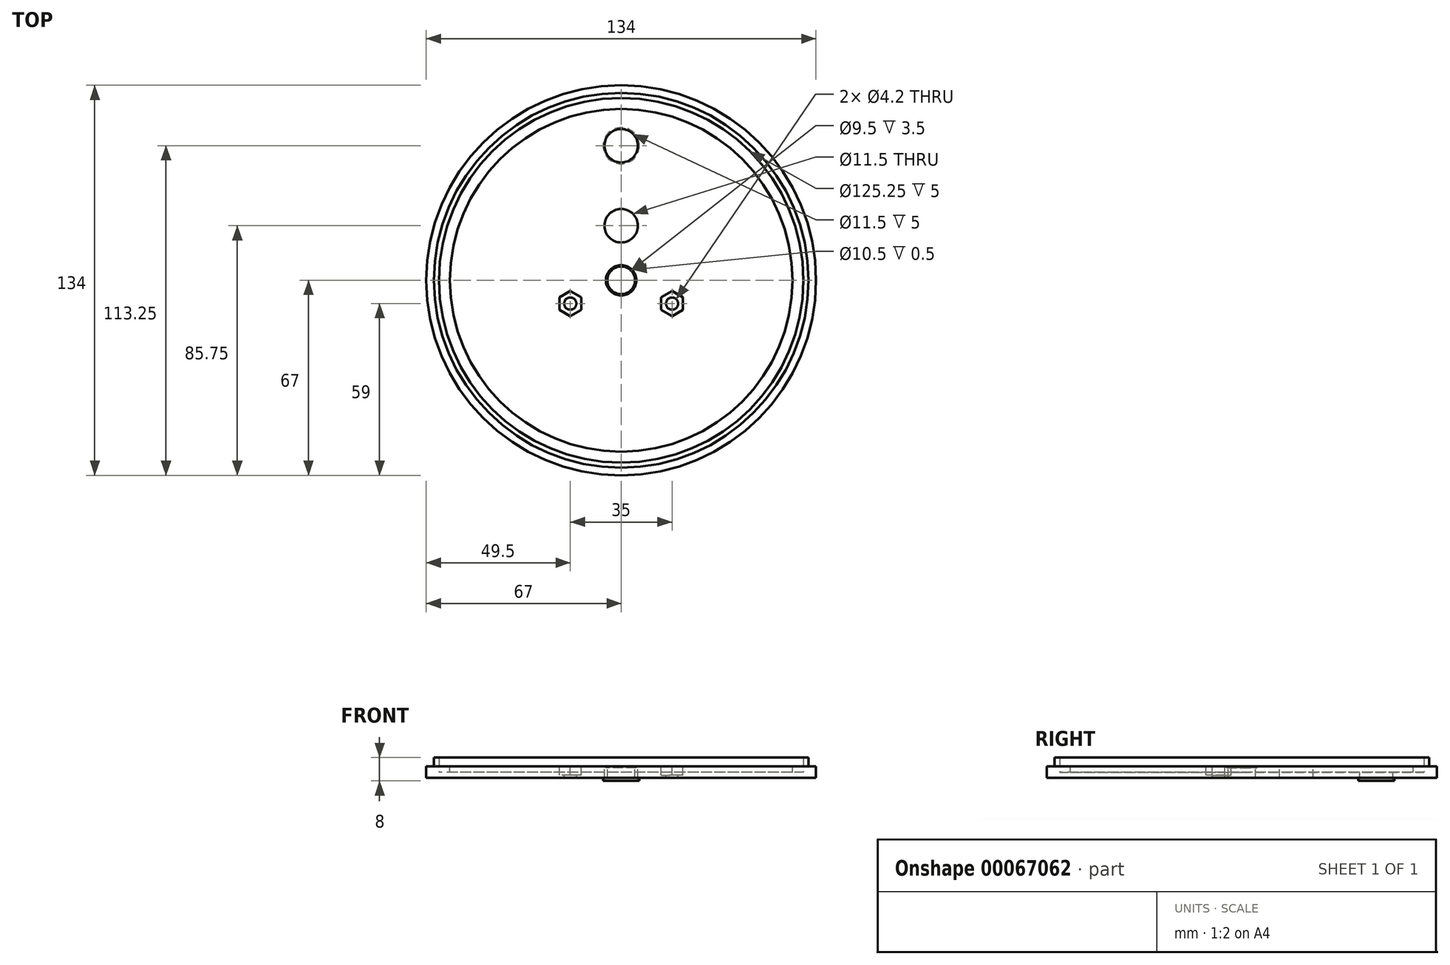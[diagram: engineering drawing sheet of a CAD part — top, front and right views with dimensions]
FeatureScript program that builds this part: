
annotation { "Feature Type Name" : "Feature", "Feature Type Description" : "" }
export const myFeature = defineFeature(function(context is Context, id is Id, definition is map)
    precondition{}
    {
        {
            var Q0;
            Q0=qCreatedBy(makeId("Top.planeOp"),FACE);
            var sketch = newSketch(context, id + "F0", { "sketchPlane" : qUnion([Q0])});
            skCircle(sketch, "E0", {"center": v(0, 0) * mm, "radius": 67 * mm});
            skSolve(sketch);
        }
        {
            var Q0;
            Q0=makeQuery(id+"F0.imprint","IMPRINT",FACE,{"disambiguationData":[TD([[makeQuery(id+"F0.imprint","IMPRINT",EDGE,{"derivedFrom":sQuery(id+"F0.wireOp",EDGE,"E0")}),1.0]])]});
            extrude(context, id + "F1", {"entities" : qUnion([Q0]), "endBound" : BoundingType.SYMMETRIC, "depth" : 5 * mm});
        }
        {
            var Q0;
            Q0=makeQuery(id+"F1.opExtrude","CAP_FACE",FACE,{"disambiguationData":[OSD([sQuery(id+"F0.wireOp",EDGE,"E0")])],"isStart":false});
            var sketch = newSketch(context, id + "F2", { "sketchPlane" : qUnion([Q0])});
            skCircle(sketch, "E1", {"center": v(0, 0) * mm, "radius": 64.38 * mm});
            skCircle(sketch, "E2", {"center": v(0, 0) * mm, "radius": 62.62 * mm});
            skCircle(sketch, "E3", {"center": v(0, 0) * mm, "radius": 58.88 * mm});
            skSolve(sketch);
        }
        {
            var Q0;
            Q0=makeQuery(id+"F2.imprint","IMPRINT",FACE,{"disambiguationData":[TD([[makeQuery(id+"F2.imprint","IMPRINT",EDGE,{"derivedFrom":sQuery(id+"F2.wireOp",EDGE,"E1")}),1.0]])]});
            var Q1;
            Q1=sQuery(id+"F2.wireOp",EDGE,"E1");
            var Q2;
            Q2=sQuery(id+"F2.wireOp",EDGE,"E2");
            extrude(context, id + "F3", {"entities" : qUnion([Q0]), "operationType" : NewBodyOperationType.ADD, "surfaceEntities" : qUnion([Q1, Q2]), "depth" : 3 * mm});
        }
        {
            var Q0;
            Q0=makeQuery(id+"F2.imprint","IMPRINT",FACE,{"disambiguationData":[TD([[makeQuery(id+"F2.imprint","IMPRINT",EDGE,{"derivedFrom":sQuery(id+"F2.wireOp",EDGE,"E2")}),1.0]])]});
            var Q1;
            Q1=sQuery(id+"F2.wireOp",EDGE,"E2");
            var Q2;
            Q2=sQuery(id+"F2.wireOp",EDGE,"E3");
            extrude(context, id + "F4", {"entities" : qUnion([Q0]), "operationType" : NewBodyOperationType.REMOVE, "surfaceEntities" : qUnion([Q1, Q2]), "oppositeDirection" : true, "depth" : 2 * mm});
        }
        {
            var Q0;
            Q0=makeQuery(id+"F2.imprint","IMPRINT",FACE,{"disambiguationData":[TD([[makeQuery(id+"F2.imprint","IMPRINT",EDGE,{"derivedFrom":sQuery(id+"F2.wireOp",EDGE,"E3")}),1.0]])]});
            var sketch = newSketch(context, id + "F5", { "sketchPlane" : qUnion([Q0])});
            skCircle(sketch, "E4", {"center": v(0, 0) * mm, "radius": 4.75 * mm});
            skCircle(sketch, "E5", {"center": v(0, 18.75) * mm, "radius": 5.75 * mm});
            skCircle(sketch, "E6", {"center": v(0, 46.25) * mm, "radius": 5.75 * mm});
            skLineSegment(sketch, "E7", {"start": v(0, -8) * mm, "end": v(17.5, -8) * mm, "construction": true});
            skCircle(sketch, "E8", {"center": v(17.5, -8) * mm, "radius": 2.1 * mm});
            skLineSegment(sketch, "E9", {"start": v(0, 0) * mm, "end": v(0, -8) * mm, "construction": true});
            skCircle(sketch, "E10.MirrorC", {"center": v(-17.5, -8) * mm, "radius": 2.1 * mm});
            skSolve(sketch);
        }
        {
            var Q0;
            Q0 = qSketchRegion(id + "F5", true);
            extrude(context, id + "F6", {"entities" : qUnion([Q0]), "operationType" : NewBodyOperationType.REMOVE, "endBound" : BoundingType.THROUGH_ALL, "oppositeDirection" : true, "depth" : 25 * mm});
        }
        {
            var Q0;
            Q0=makeQuery(id+"F2.imprint","IMPRINT",FACE,{"disambiguationData":[TD([[makeQuery(id+"F2.imprint","IMPRINT",EDGE,{"derivedFrom":sQuery(id+"F2.wireOp",EDGE,"E3")}),1.0]])]});
            var sketch = newSketch(context, id + "F7", { "sketchPlane" : qUnion([Q0])});
            skCircle(sketch, "E11", {"center": v(0, 46.25) * mm, "radius": 6.25 * mm});
            skCircle(sketch, "E12", {"center": v(0, 18.75) * mm, "radius": 6.25 * mm});
            skCircle(sketch, "E13", {"center": v(0, 0) * mm, "radius": 5.25 * mm});
            skCircle(sketch, "E14.cCircle", {"center": v(17.5, -8) * mm, "radius": 3.75 * mm, "construction": true});
            skLineSegment(sketch, "E14.0", {"start": v(21.25, -10.17) * mm, "end": v(17.5, -12.33) * mm});
            skLineSegment(sketch, "E14.1", {"start": v(17.5, -12.33) * mm, "end": v(13.75, -10.17) * mm});
            skLineSegment(sketch, "E14.2", {"start": v(13.75, -10.17) * mm, "end": v(13.75, -5.83) * mm});
            skLineSegment(sketch, "E14.3", {"start": v(13.75, -5.83) * mm, "end": v(17.5, -3.67) * mm});
            skLineSegment(sketch, "E14.4", {"start": v(17.5, -3.67) * mm, "end": v(21.25, -5.83) * mm});
            skLineSegment(sketch, "E14.5", {"start": v(21.25, -5.83) * mm, "end": v(21.25, -10.17) * mm});
            skPoint(sketch, "E14.0.midPoint", {"position": v(19.38, -11.25) * mm});
            skLineSegment(sketch, "E15.MirrorCS", {"start": v(-13.75, -5.83) * mm, "end": v(-17.5, -3.67) * mm});
            skLineSegment(sketch, "E16.MirrorCS", {"start": v(-13.75, -10.17) * mm, "end": v(-13.75, -5.83) * mm});
            skLineSegment(sketch, "E17.MirrorCS", {"start": v(-17.5, -3.67) * mm, "end": v(-21.25, -5.83) * mm});
            skLineSegment(sketch, "E18.MirrorCS", {"start": v(-21.25, -5.83) * mm, "end": v(-21.25, -10.17) * mm});
            skLineSegment(sketch, "E19.MirrorCS", {"start": v(-17.5, -12.33) * mm, "end": v(-13.75, -10.17) * mm});
            skLineSegment(sketch, "E20.MirrorCS", {"start": v(-21.25, -10.17) * mm, "end": v(-17.5, -12.33) * mm});
            skCircle(sketch, "E21.0", {"center": v(0, 46.25) * mm, "radius": 5.75 * mm});
            skCircle(sketch, "E22.0", {"center": v(0, 18.75) * mm, "radius": 5.75 * mm});
            skCircle(sketch, "E23.0", {"center": v(0, 0) * mm, "radius": 4.75 * mm});
            skCircle(sketch, "E24.0", {"center": v(-17.5, -8) * mm, "radius": 2.1 * mm});
            skCircle(sketch, "E25.0.0", {"center": v(0, 0) * mm, "radius": 58.88 * mm});
            skCircle(sketch, "E26.0", {"center": v(17.5, -8) * mm, "radius": 2.1 * mm});
            skSolve(sketch);
        }
        {
            var Q0;
            Q0=makeQuery(id+"F7.imprint","IMPRINT",FACE,{"disambiguationData":[TD([[makeQuery(id+"F7.imprint","IMPRINT",EDGE,{"derivedFrom":sQuery(id+"F7.wireOp",EDGE,"E13")}),1.0]])]});
            extrude(context, id + "F8", {"entities" : qUnion([Q0]), "operationType" : NewBodyOperationType.REMOVE, "oppositeDirection" : true, "depth" : 0.5 * mm});
        }
        {
            var Q0;
            Q0=makeQuery(id+"F7.imprint","IMPRINT",FACE,{"disambiguationData":[TD([[makeQuery(id+"F7.imprint","IMPRINT",EDGE,{"derivedFrom":sQuery(id+"F7.wireOp",EDGE,"E15.MirrorCS")}),1.0]])]});
            var Q1;
            Q1=makeQuery(id+"F7.imprint","IMPRINT",FACE,{"disambiguationData":[TD([[makeQuery(id+"F7.imprint","IMPRINT",EDGE,{"derivedFrom":sQuery(id+"F7.wireOp",EDGE,"E24.0")}),-1.0]])]});
            extrude(context, id + "F9", {"entities" : qUnion([Q0, Q1]), "operationType" : NewBodyOperationType.REMOVE, "oppositeDirection" : true, "depth" : 3 * mm});
        }
        {
            var Q0;
            Q0=makeQuery(id+"F7.imprint","IMPRINT",FACE,{"disambiguationData":[TD([[makeQuery(id+"F7.imprint","IMPRINT",EDGE,{"derivedFrom":sQuery(id+"F7.wireOp",EDGE,"E14.0")}),-1.0]])]});
            var Q1;
            Q1=makeQuery(id+"F7.imprint","IMPRINT",FACE,{"disambiguationData":[TD([[makeQuery(id+"F7.imprint","IMPRINT",EDGE,{"derivedFrom":sQuery(id+"F7.wireOp",EDGE,"E26.0")}),1.0]])]});
            extrude(context, id + "F10", {"entities" : qUnion([Q0, Q1]), "operationType" : NewBodyOperationType.REMOVE, "oppositeDirection" : true, "depth" : 3 * mm});
        }
        {
            var Q0;
            Q0=makeQuery(id+"F1.opExtrude","CAP_FACE",FACE,{"disambiguationData":[OSD([sQuery(id+"F0.wireOp",EDGE,"E0")])],"isStart":true});
            var sketch = newSketch(context, id + "F11", { "sketchPlane" : qUnion([Q0])});
            skCircle(sketch, "E27", {"center": v(0, -46.25) * mm, "radius": 6.25 * mm});
            skCircle(sketch, "E28", {"center": v(0, -18.75) * mm, "radius": 6.25 * mm});
            skCircle(sketch, "E29.0", {"center": v(0, -18.75) * mm, "radius": 5.75 * mm});
            skCircle(sketch, "E30.0", {"center": v(0, -46.25) * mm, "radius": 5.75 * mm});
            skSolve(sketch);
        }
        {
            var Q0;
            Q0=makeQuery(id+"F11.imprint","IMPRINT",FACE,{"disambiguationData":[TD([[makeQuery(id+"F11.imprint","IMPRINT",EDGE,{"derivedFrom":sQuery(id+"F11.wireOp",EDGE,"E27")}),-1.0]])]});
            var Q1;
            Q1=makeQuery(id+"F11.imprint","IMPRINT",FACE,{"disambiguationData":[TD([[makeQuery(id+"F11.imprint","IMPRINT",EDGE,{"derivedFrom":sQuery(id+"F11.wireOp",EDGE,"E28")}),1.0]])]});
            extrude(context, id + "F12", {"entities" : qUnion([Q0, Q1]), "operationType" : NewBodyOperationType.REMOVE, "oppositeDirection" : true, "depth" : 1 * mm});
        }
    });
